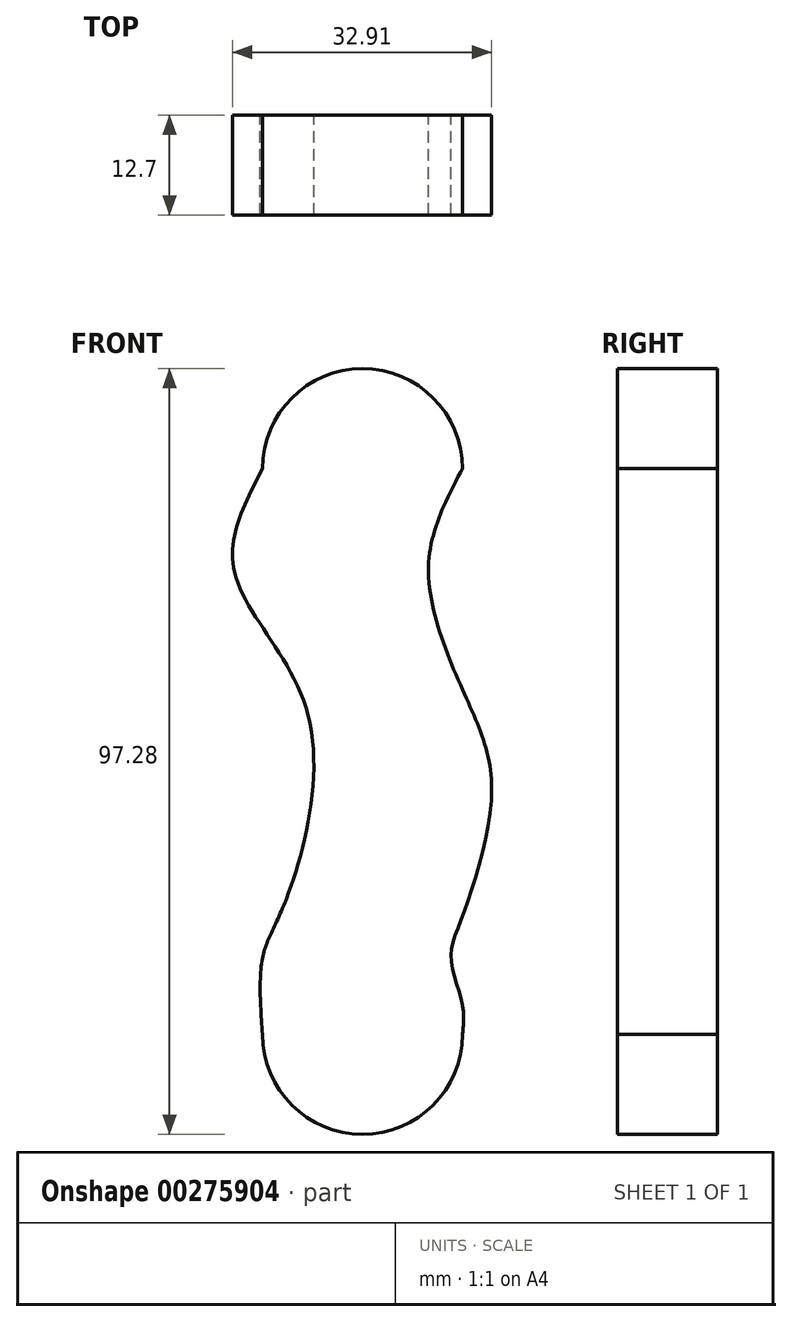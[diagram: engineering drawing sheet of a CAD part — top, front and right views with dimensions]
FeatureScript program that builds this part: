
annotation { "Feature Type Name" : "Feature", "Feature Type Description" : "" }
export const myFeature = defineFeature(function(context is Context, id is Id, definition is map)
    precondition{}
    {
        {
            var Q0;
            Q0=qCreatedBy(makeId("Front.planeOp"),FACE);
            var sketch = newSketch(context, id + "F0", { "sketchPlane" : qUnion([Q0])});
            skPoint(sketch, "E0", {"position": v(0, 50.8) * mm});
            skArc(sketch, "E1", {"start": v(12.7, 50.8) * mm, "mid": v(0, 63.5) * mm, "end": v(-12.7, 50.8) * mm});
            skLineSegment(sketch, "E2", {"start": v(-12.7, 50.8) * mm, "end": v(12.7, 50.8) * mm});
            skFitSpline(sketch, "E3", {"points": [v(-12.7, 50.8) * mm, v(-16.25, 37.67) * mm, v(-6.91, 19.5) * mm, v(-9.97, -4.61) * mm, v(-12.7, -11.4) * mm, v(-12.7, -21.08) * mm], "startDerivative": vector(-35.15, -67.45) * mm, "endDerivative": vector(4.74, -64.84) * mm});
            skArc(sketch, "E4", {"start": v(12.7, -21.08) * mm, "mid": v(0, -33.78) * mm, "end": v(-12.7, -21.08) * mm});
            skLineSegment(sketch, "E5", {"start": v(12.7, -21.08) * mm, "end": v(-12.7, -21.08) * mm});
            skFitSpline(sketch, "E6", {"points": [v(12.7, -21.08) * mm, v(12.7, -17.36) * mm, v(11.26, -11.62) * mm, v(12.7, -6.02) * mm, v(16.4, 10.17) * mm, v(12.7, 22.72) * mm, v(8.39, 38.3) * mm, v(12.7, 50.8) * mm], "startDerivative": vector(4.54, 39.8) * mm, "endDerivative": vector(38.31, 72.45) * mm});
            skLineSegment(sketch, "E7", {"start": v(-9.97, -4.61) * mm, "end": v(16.4, 10.17) * mm});
            skLineSegment(sketch, "E8", {"start": v(12.7, 22.72) * mm, "end": v(-6.91, 19.5) * mm});
            skLineSegment(sketch, "E9", {"start": v(8.39, 38.3) * mm, "end": v(-16.25, 37.67) * mm});
            skLineSegment(sketch, "E10", {"start": v(-12.7, -11.4) * mm, "end": v(12.7, -17.36) * mm});
            skSolve(sketch);
        }
        {
            var Q0;
            Q0 = qSketchRegion(id + "F0", true);
            extrude(context, id + "F1", {"entities" : qUnion([Q0]), "depth" : 12.7 * mm});
        }
    });
